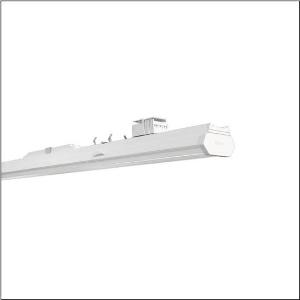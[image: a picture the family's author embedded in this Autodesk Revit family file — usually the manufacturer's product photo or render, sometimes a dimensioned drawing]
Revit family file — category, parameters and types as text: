
# Revit family: licross_r__11_protected_mo_51tp12dn695g_2e2e
name_source: partatom
category: Lighting Fixtures
units: mm (PartAtom-declared; Revit-internal decimal feet)

## family parameters
Cut with Voids When Loaded = No
Host = Face
Light Source = No
Part Type = Normal
Room Calculation Point = No
Round Connector Dimension = Use Diameter
Shared = No

## types (1)
- --- (1 x LED, 9730 lm, 57.1 W, 6500K)
    Apparent Load = 57 VA
    CIE Flux Codes = 73 92 98 99 100
    Color Rendering = 80
    Color Temperature = 6500K
    Default Elevation = 1800 mm
    Description = Licross® 11 Protected MO, luminaire insert, of sheet steel, galvanised, coil coated, white, length: 1.500mm, width: 90mm, height: 101mm, LED rated luminous flux: 9.730lm, light colour: 865, control gear: DALI 2, with plug, 5-pole, with phase selection, mains connection: 220..240V, AC, 50/60Hz, rated input power: 57W, halogen-free wiring, primary optical cover: cover, of PMMA, light emission: direct distribution, primary light characteristic: symmetric, protection rating (complete): IP64, insulation class (complete): insulation class I (protective earthing), certification: CE, ENEC, VDE, UKCA, protection symbol: D if used in an environment with conductive dust loads with corresponding accessories, impact resistance: IK06, permissible ambient temperature for indoor applications: -25..+35°C, corresponds to IFS (International Featured Standards) requirements for safety and quality in the food industry, reducing of maximum allowable ambient temperature of 5°C with ceiling mounting, LABS conformity tested according to VDMA 24364:2018-05, packaging unit: 1 piece
    Height = 92 mm
    Lamp = 1 x LED
    Lamp Light Flux = 9730 lm
    Lamp Power = 57.1 W
    Lamp count = 1
    Length = 1500 mm
    Luminous efficacy = 170 lm/W
    Manufacturer = Siteco
    ModVariant = No
    Model = 51TP12DN695G
    Mounting Place = Ceiling
    Mounting Type = Pendant
    Number of Poles = 1
    OnlyDefault = Yes
    Power Factor = 1
    Product Name = Licross® 11 Protected MO
    Product group = luminaire insert
    ProductGroupID = 901
    Protection Class = Protection class I
    Protection Degree = IP 64
    RLX_Detail_Level = 1
    RLX_Emergency_Light_Flux = 0 lm
    RLX_Emergency_Type = 0
    RLX_Emergency_Type_DB = No
    RlxData = <blob elided: 24353 chars, md5=a0023e69>
    Socket = socket
    Standby Power = 0 W
    System Light Flux = 9730 lm
    System Power = 57 W
    Type Comments = factory setting: luminous flux: 100 % | dim-lin: 254 | 378 mA
    Type Image = l_1256148.jpg
    URL = http://relux.com
    VarID = @adj_028501
    Voltage = 0 V
    Weight = 0.00 kg
    Width = 88 mm

## geometry (parser evidence)
native form markers: Blend x4, Sweep x11
no freeform markers — native parametric forms only
